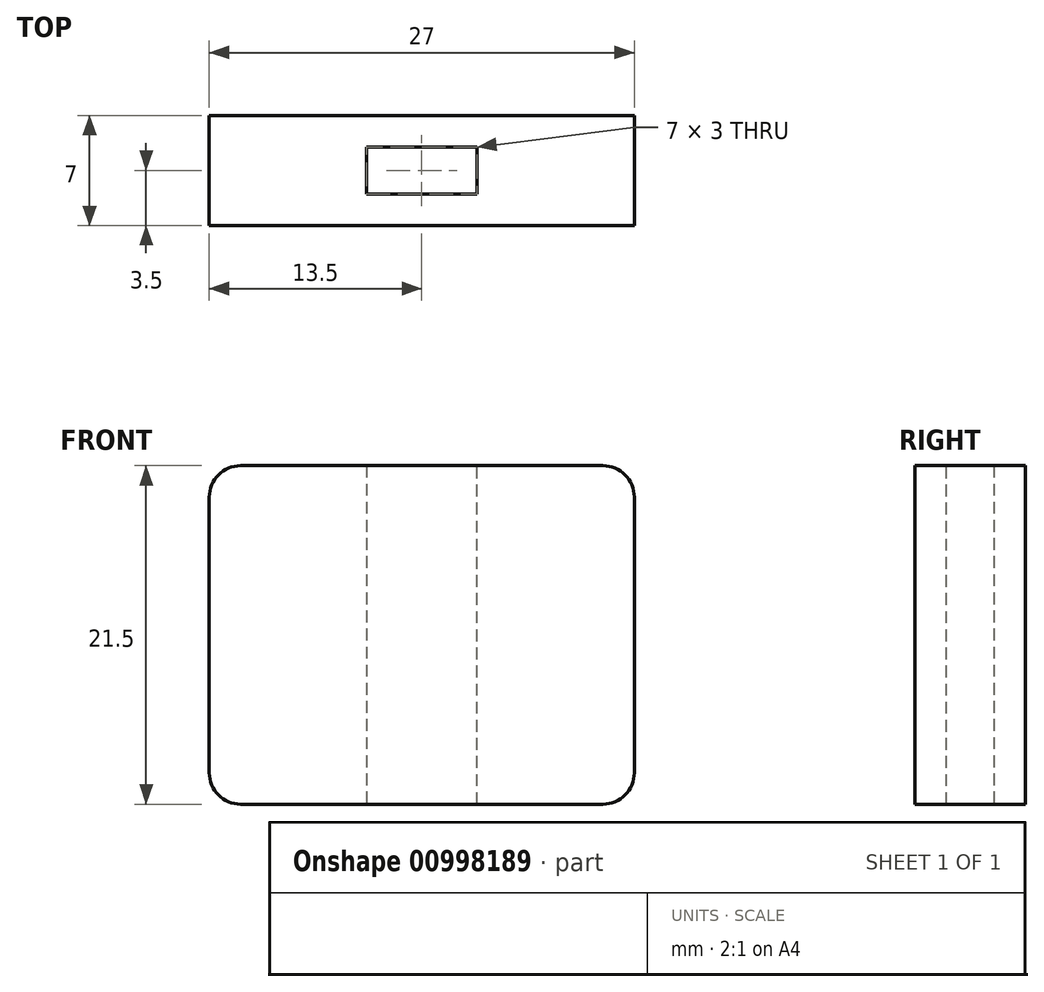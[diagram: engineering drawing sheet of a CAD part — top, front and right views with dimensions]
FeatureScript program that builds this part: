
annotation { "Feature Type Name" : "Feature", "Feature Type Description" : "" }
export const myFeature = defineFeature(function(context is Context, id is Id, definition is map)
    precondition{}
    {
        {
            var Q0;
            Q0=qCreatedBy(makeId("Front.planeOp"),FACE);
            var sketch = newSketch(context, id + "F0", { "sketchPlane" : qUnion([Q0])});
            skLineSegment(sketch, "E0.bottom", {"start": v(-2, 0) * mm, "end": v(-25, 0) * mm});
            skLineSegment(sketch, "E0.top", {"start": v(-2, 21.5) * mm, "end": v(-25, 21.5) * mm});
            skLineSegment(sketch, "E0.left", {"start": v(0, 2) * mm, "end": v(0, 19.5) * mm});
            skLineSegment(sketch, "E0.right", {"start": v(-27, 2) * mm, "end": v(-27, 19.5) * mm});
            skPoint(sketch, "E1.visualSharp", {"position": v(-27, 21.5) * mm});
            skArc(sketch, "E1.filletArc", {"start": v(-25, 21.5) * mm, "mid": v(-26.41, 20.91) * mm, "end": v(-27, 19.5) * mm});
            skPoint(sketch, "E2.visualSharp", {"position": v(0, 21.5) * mm});
            skArc(sketch, "E2.filletArc", {"start": v(0, 19.5) * mm, "mid": v(-0.59, 20.91) * mm, "end": v(-2, 21.5) * mm});
            skPoint(sketch, "E3.visualSharp", {"position": v(-27, 0) * mm});
            skArc(sketch, "E3.filletArc", {"start": v(-27, 2) * mm, "mid": v(-26.41, 0.59) * mm, "end": v(-25, 0) * mm});
            skPoint(sketch, "E4.visualSharp", {"position": v(0, 0) * mm});
            skArc(sketch, "E4.filletArc", {"start": v(-2, 0) * mm, "mid": v(-0.59, 0.59) * mm, "end": v(0, 2) * mm});
            skSolve(sketch);
        }
        {
            var Q0;
            Q0=makeQuery(id+"F0.imprint","IMPRINT",FACE,{"disambiguationData":[TD([[makeQuery(id+"F0.imprint","IMPRINT",EDGE,{"derivedFrom":sQuery(id+"F0.wireOp",EDGE,"E0.bottom")}),-1.0]])]});
            extrude(context, id + "F1", {"entities" : qUnion([Q0]), "depth" : 2 * mm, "offsetDistance" : 25 * mm});
        }
        {
            var Q0;
            Q0=makeQuery(id+"F1.opExtrude","CAP_FACE",FACE,{"disambiguationData":[OSD([sQuery(id+"F0.wireOp",EDGE,"E0.bottom"),sQuery(id+"F0.wireOp",EDGE,"E0.top"),sQuery(id+"F0.wireOp",EDGE,"E0.left"),sQuery(id+"F0.wireOp",EDGE,"E0.right"),sQuery(id+"F0.wireOp",EDGE,"E1.filletArc"),sQuery(id+"F0.wireOp",EDGE,"E2.filletArc"),sQuery(id+"F0.wireOp",EDGE,"E3.filletArc"),sQuery(id+"F0.wireOp",EDGE,"E4.filletArc")])],"isStart":false});
            var sketch = newSketch(context, id + "F2", { "sketchPlane" : qUnion([Q0])});
            skLineSegment(sketch, "E5.bottom", {"start": v(-2, 0) * mm, "end": v(-10, 0) * mm});
            skLineSegment(sketch, "E5.top", {"start": v(-2, 21.5) * mm, "end": v(-10, 21.5) * mm});
            skLineSegment(sketch, "E5.left", {"start": v(0, 2) * mm, "end": v(0, 19.5) * mm});
            skLineSegment(sketch, "E5.right", {"start": v(-10, 0) * mm, "end": v(-10, 21.5) * mm});
            skPoint(sketch, "E6.left.start.orphan", {"position": v(-26.41, 0.59) * mm});
            skPoint(sketch, "E7.visualSharp", {"position": v(0, 21.5) * mm});
            skArc(sketch, "E7.filletArc", {"start": v(0, 19.5) * mm, "mid": v(-0.59, 20.91) * mm, "end": v(-2, 21.5) * mm});
            skPoint(sketch, "E8.visualSharp", {"position": v(0, 0) * mm});
            skArc(sketch, "E8.filletArc", {"start": v(-2, 0) * mm, "mid": v(-0.59, 0.59) * mm, "end": v(0, 2) * mm});
            skLineSegment(sketch, "E9.bottom", {"start": v(-25, 21.5) * mm, "end": v(-17, 21.5) * mm});
            skLineSegment(sketch, "E9.top", {"start": v(-25, 0) * mm, "end": v(-17, 0) * mm});
            skLineSegment(sketch, "E9.left", {"start": v(-27, 19.5) * mm, "end": v(-27, 2) * mm});
            skLineSegment(sketch, "E9.right", {"start": v(-17, 21.5) * mm, "end": v(-17, 0) * mm});
            skPoint(sketch, "E10.visualSharp", {"position": v(-27, 21.5) * mm});
            skArc(sketch, "E10.filletArc", {"start": v(-25, 21.5) * mm, "mid": v(-26.41, 20.91) * mm, "end": v(-27, 19.5) * mm});
            skPoint(sketch, "E11.visualSharp", {"position": v(-27, 0) * mm});
            skArc(sketch, "E11.filletArc", {"start": v(-27, 2) * mm, "mid": v(-26.41, 0.59) * mm, "end": v(-25, 0) * mm});
            skSolve(sketch);
        }
        {
            var Q0;
            Q0=makeQuery(id+"F2.imprint","IMPRINT",FACE,{"disambiguationData":[TD([[makeQuery(id+"F2.imprint","IMPRINT",EDGE,{"derivedFrom":sQuery(id+"F2.wireOp",EDGE,"E9.bottom")}),1.0]])]});
            var Q1;
            Q1=makeQuery(id+"F2.imprint","IMPRINT",FACE,{"disambiguationData":[TD([[makeQuery(id+"F2.imprint","IMPRINT",EDGE,{"derivedFrom":sQuery(id+"F2.wireOp",EDGE,"E5.bottom")}),-1.0]])]});
            extrude(context, id + "F3", {"entities" : qUnion([Q0, Q1]), "operationType" : NewBodyOperationType.ADD, "depth" : 3 * mm, "offsetDistance" : 25 * mm});
        }
        {
            var Q0;
            Q0=makeQuery(id+"F3.opExtrude","CAP_FACE",FACE,{"disambiguationData":[OSD([sQuery(id+"F2.wireOp",EDGE,"E9.bottom"),sQuery(id+"F2.wireOp",EDGE,"E9.top"),sQuery(id+"F2.wireOp",EDGE,"E9.left"),sQuery(id+"F2.wireOp",EDGE,"E9.right"),sQuery(id+"F2.wireOp",EDGE,"E10.filletArc"),sQuery(id+"F2.wireOp",EDGE,"E11.filletArc")])],"isStart":false});
            var sketch = newSketch(context, id + "F4", { "sketchPlane" : qUnion([Q0])});
            skLineSegment(sketch, "E12.bottom", {"start": v(-25, 21.5) * mm, "end": v(-2, 21.5) * mm});
            skLineSegment(sketch, "E12.top", {"start": v(-25, 0) * mm, "end": v(-2, 0) * mm});
            skLineSegment(sketch, "E12.left", {"start": v(-27, 19.5) * mm, "end": v(-27, 2) * mm});
            skLineSegment(sketch, "E12.right", {"start": v(0, 19.5) * mm, "end": v(0, 2) * mm});
            skPoint(sketch, "E13.visualSharp", {"position": v(-27, 21.5) * mm});
            skArc(sketch, "E13.filletArc", {"start": v(-25, 21.5) * mm, "mid": v(-26.41, 20.91) * mm, "end": v(-27, 19.5) * mm});
            skPoint(sketch, "E14.visualSharp", {"position": v(0, 21.5) * mm});
            skArc(sketch, "E14.filletArc", {"start": v(0, 19.5) * mm, "mid": v(-0.59, 20.91) * mm, "end": v(-2, 21.5) * mm});
            skPoint(sketch, "E15.visualSharp", {"position": v(0, 0) * mm});
            skArc(sketch, "E15.filletArc", {"start": v(-2, 0) * mm, "mid": v(-0.59, 0.59) * mm, "end": v(0, 2) * mm});
            skPoint(sketch, "E16.visualSharp", {"position": v(-27, 0) * mm});
            skArc(sketch, "E16.filletArc", {"start": v(-27, 2) * mm, "mid": v(-26.41, 0.59) * mm, "end": v(-25, 0) * mm});
            skSolve(sketch);
        }
        {
            var Q0;
            Q0=makeQuery(id+"F4.imprint","IMPRINT",FACE,{"disambiguationData":[TD([[makeQuery(id+"F4.imprint","IMPRINT",EDGE,{"derivedFrom":sQuery(id+"F4.wireOp",EDGE,"E12.left")}),-1.0]])]});
            var Q1;
            Q1=makeQuery(id+"F4.imprint","IMPRINT",FACE,{"disambiguationData":[TD([[makeQuery(id+"F4.imprint","IMPRINT",EDGE,{"derivedFrom":sQuery(id+"F4.wireOp",EDGE,"E12.right")}),-1.0]])]});
            extrude(context, id + "F5", {"entities" : qUnion([Q0, Q1]), "operationType" : NewBodyOperationType.ADD, "depth" : 2 * mm, "offsetDistance" : 25 * mm});
        }
    });
